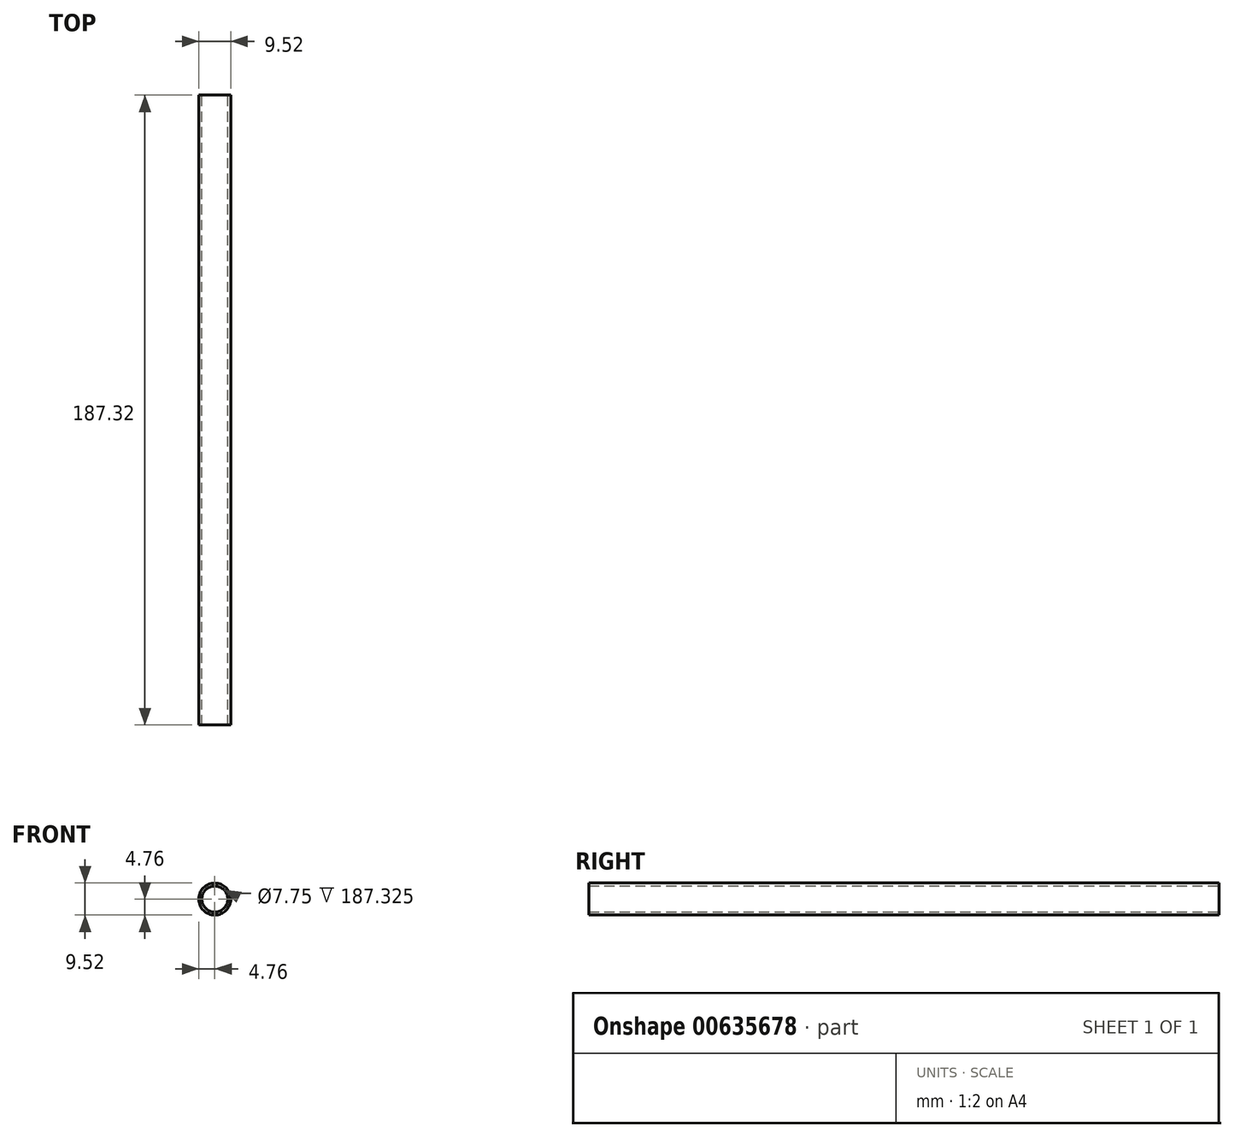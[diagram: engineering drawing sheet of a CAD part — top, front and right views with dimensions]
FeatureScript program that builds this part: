
annotation { "Feature Type Name" : "Feature", "Feature Type Description" : "" }
export const myFeature = defineFeature(function(context is Context, id is Id, definition is map)
    precondition{}
    {
        {
            var Q0;
            Q0=qCreatedBy(makeId("Front.planeOp"),FACE);
            var sketch = newSketch(context, id + "F0", { "sketchPlane" : qUnion([Q0])});
            skCircle(sketch, "E0", {"center": v(0, 0) * mm, "radius": 4.76 * mm});
            skCircle(sketch, "E1", {"center": v(0, 0) * mm, "radius": 3.87 * mm});
            skSolve(sketch);
        }
        {
            var Q0;
            Q0 = qSketchRegion(id + "F0", true);
            extrude(context, id + "F1", {"entities" : qUnion([Q0]), "endBound" : BoundingType.SYMMETRIC, "depth" : 187.32 * mm, "offsetDistance" : 25.4 * mm});
        }
    });
